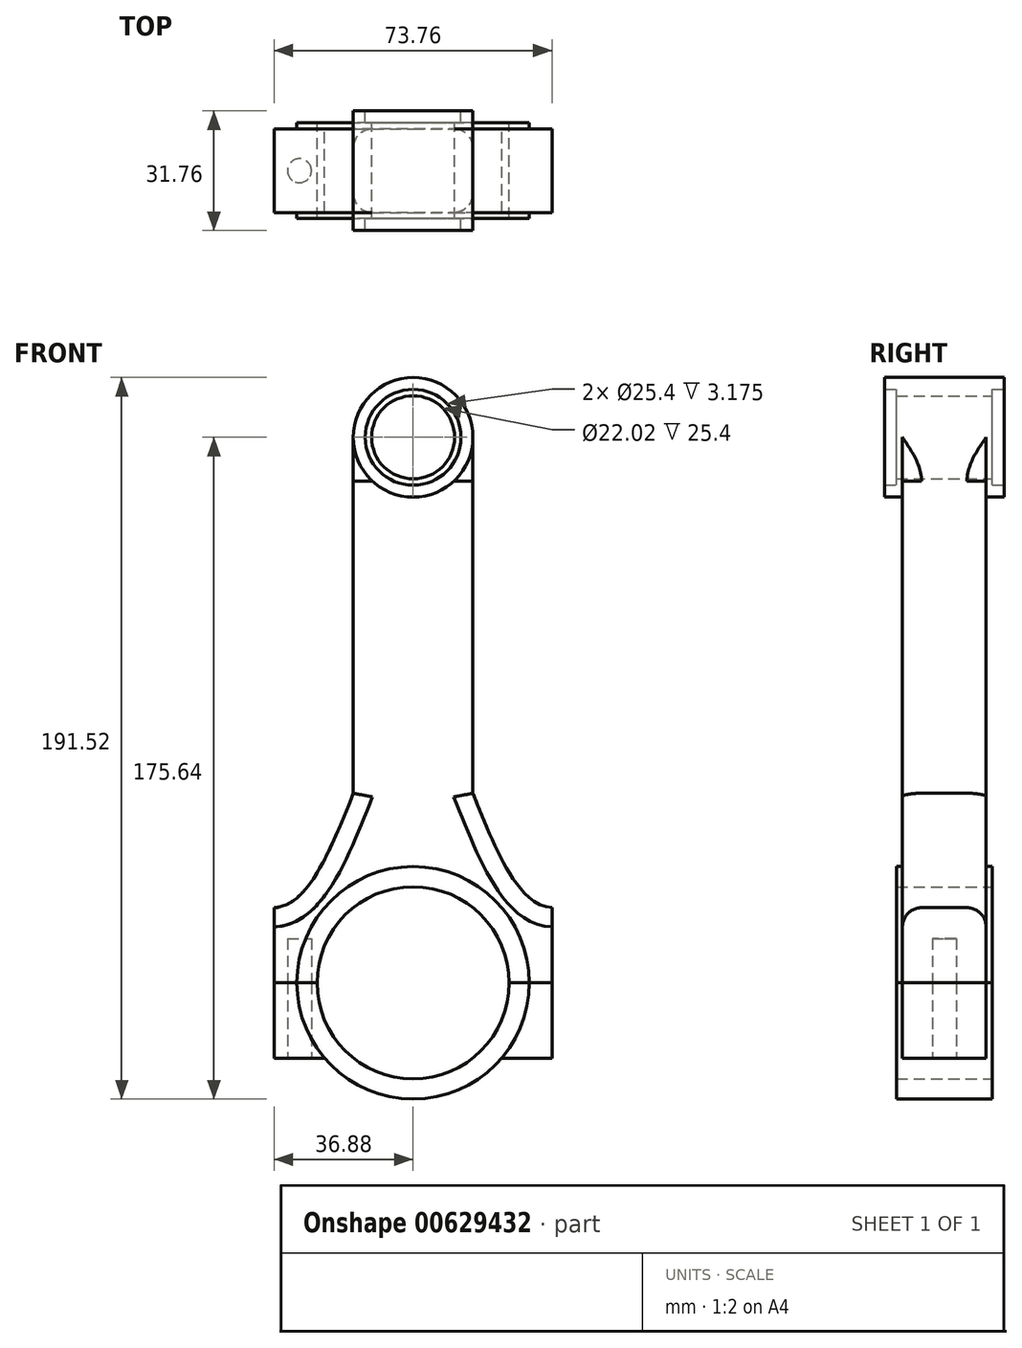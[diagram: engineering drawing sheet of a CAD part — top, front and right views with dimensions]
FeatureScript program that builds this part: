
annotation { "Feature Type Name" : "Feature", "Feature Type Description" : "" }
export const myFeature = defineFeature(function(context is Context, id is Id, definition is map)
    precondition{}
    {
        {
            var Q0;
            Q0=qCreatedBy(makeId("Front.planeOp"),FACE);
            var sketch = newSketch(context, id + "F0", { "sketchPlane" : qUnion([Q0])});
            skCircle(sketch, "E0", {"center": v(0, 0) * mm, "radius": 25.5 * mm});
            skCircle(sketch, "E1", {"center": v(0, 144.78) * mm, "radius": 11.01 * mm});
            skCircle(sketch, "E2", {"center": v(0, 144.78) * mm, "radius": 12.7 * mm});
            skCircle(sketch, "E3", {"center": v(0, 144.78) * mm, "radius": 15.88 * mm});
            skLineSegment(sketch, "E4", {"start": v(15.88, 144.78) * mm, "end": v(15.88, 50.32) * mm});
            skLineSegment(sketch, "E5", {"start": v(-15.88, 144.78) * mm, "end": v(-15.87, 50.32) * mm});
            skLineSegment(sketch, "E6.top", {"start": v(32.06, -19.96) * mm, "end": v(23.54, -19.96) * mm});
            skCircle(sketch, "E7", {"center": v(0, 0) * mm, "radius": 30.86 * mm});
            skPoint(sketch, "E8.orphan", {"position": v(15.88, 19.96) * mm});
            skLineSegment(sketch, "E9.trimOffspring", {"start": v(-23.54, -19.96) * mm, "end": v(-32.06, -19.96) * mm});
            skLineSegment(sketch, "E10.bottom", {"start": v(36.88, -19.96) * mm, "end": v(23.54, -19.96) * mm});
            skLineSegment(sketch, "E10.left", {"start": v(36.88, -19.96) * mm, "end": v(36.88, 19.96) * mm});
            skLineSegment(sketch, "E10.right", {"start": v(-36.88, -19.96) * mm, "end": v(-36.88, 19.96) * mm});
            skPoint(sketch, "E6.right.start.orphan", {"position": v(-32.06, 19.96) * mm});
            skFitSpline(sketch, "E11", {"points": [v(-15.87, 50.32) * mm, v(-36.88, 19.96) * mm, v(-54.21, 32.97) * mm, v(-52.7, 39.53) * mm], "startDerivative": vector(-39.39, -98.54) * mm, "endDerivative": vector(18.96, 28.68) * mm});
            skFitSpline(sketch, "E12.MirrorCS", {"points": [v(15.87, 50.32) * mm, v(36.88, 19.96) * mm, v(54.21, 32.97) * mm, v(52.7, 39.53) * mm], "startDerivative": vector(39.39, -98.54) * mm, "endDerivative": vector(-18.96, 28.68) * mm});
            skPoint(sketch, "E13.1.internal.orphan", {"position": v(32.06, 19.96) * mm});
            skPoint(sketch, "E13.2.internal.orphan", {"position": v(59.54, 19.96) * mm});
            skLineSegment(sketch, "E14.trimOffspring", {"start": v(-23.54, -19.96) * mm, "end": v(-36.88, -19.96) * mm});
            skSolve(sketch);
        }
        {
            var Q0;
            Q0=makeQuery(id+"F0.imprint","IMPRINT",FACE,{"disambiguationData":[TD([[makeQuery(id+"F0.imprint","IMPRINT",EDGE,{"derivedFrom":sQuery(id+"F0.wireOp",EDGE,"E0")}),-1.0]])]});
            extrude(context, id + "F1", {"entities" : qUnion([Q0]), "depth" : 25.4 * mm, "offsetDistance" : 25.4 * mm, "symmetric" : true});
        }
        {
            var Q0;
            {var subQ6=sQuery(id+"F0.wireOp",EDGE,"E4");Q0=makeQuery(id+"F0.imprint","IMPRINT",FACE,{"disambiguationData":[TD([[makeQuery(id+"F0.imprint","IMPRINT",EDGE,{"derivedFrom":subQ6}),-1.0]])]});}
            extrude(context, id + "F2", {"entities" : qUnion([Q0]), "operationType" : NewBodyOperationType.ADD, "depth" : 22.22 * mm, "offsetDistance" : 25.4 * mm, "symmetric" : true});
        }
        {
            var Q0;
            Q0=makeQuery(id+"F0.imprint","IMPRINT",FACE,{"disambiguationData":[TD([[makeQuery(id+"F0.imprint","IMPRINT",EDGE,{"derivedFrom":sQuery(id+"F0.wireOp",EDGE,"E2")}),-1.0]])]});
            extrude(context, id + "F3", {"entities" : qUnion([Q0]), "operationType" : NewBodyOperationType.ADD, "depth" : 31.75 * mm, "offsetDistance" : 25.4 * mm, "symmetric" : true});
        }
        {
            var Q0;
            Q0=makeQuery(id+"F0.imprint","IMPRINT",FACE,{"disambiguationData":[TD([[makeQuery(id+"F0.imprint","IMPRINT",EDGE,{"derivedFrom":sQuery(id+"F0.wireOp",EDGE,"E1")}),-1.0]])]});
            extrude(context, id + "F4", {"entities" : qUnion([Q0]), "operationType" : NewBodyOperationType.ADD, "depth" : 25.4 * mm, "offsetDistance" : 25.4 * mm, "symmetric" : true});
        }
        {
            var Q0;
            Q0=makeQuery(id+"F2.opExtrude","CAP_EDGE",EDGE,{"disambiguationData":[OSD([sQuery(id+"F0.wireOp",EDGE,"E5")])],"isStart":false});
            var Q1;
            Q1=makeQuery(id+"F2.opExtrude","CAP_EDGE",EDGE,{"disambiguationData":[OSD([sQuery(id+"F0.wireOp",EDGE,"E5")])],"isStart":true});
            var Q2;
            Q2=makeQuery(id+"F2.opExtrude","CAP_EDGE",EDGE,{"disambiguationData":[OSD([sQuery(id+"F0.wireOp",EDGE,"E4")])],"isStart":false});
            var Q3;
            Q3=makeQuery(id+"F2.opExtrude","CAP_EDGE",EDGE,{"disambiguationData":[OSD([sQuery(id+"F0.wireOp",EDGE,"E4")])],"isStart":true});
            var Q4;
            Q4=makeQuery(id+"F2.opExtrude","CAP_EDGE",EDGE,{"disambiguationData":[OSD([sQuery(id+"F0.wireOp",EDGE,"E11")])],"isStart":false});
            var Q5;
            Q5=makeQuery(id+"F2.opExtrude","CAP_EDGE",EDGE,{"disambiguationData":[OSD([sQuery(id+"F0.wireOp",EDGE,"E11")])],"isStart":true});
            var Q6;
            Q6=makeQuery(id+"F2.opExtrude","CAP_EDGE",EDGE,{"disambiguationData":[OSD([sQuery(id+"F0.wireOp",EDGE,"E12.MirrorCS")])],"isStart":true});
            var Q7;
            Q7=makeQuery(id+"F2.opExtrude","CAP_EDGE",EDGE,{"disambiguationData":[OSD([sQuery(id+"F0.wireOp",EDGE,"E12.MirrorCS")])],"isStart":false});
            fillet(context, id + "F5", {"entities" : qUnion([Q0, Q1, Q2, Q3, Q4, Q5, Q6, Q7]), "radius" : 5.08 * mm, "tangentPropagation" : true, "allowEdgeOverflow" : false});
        }
        {
            var Q0;
            Q0=makeQuery(id+"F2.opExtrude","SWEPT_FACE",FACE,{"disambiguationData":[OSD([sQuery(id+"F0.wireOp",EDGE,"E14.trimOffspring")])]});
            var sketch = newSketch(context, id + "F6", { "sketchPlane" : qUnion([Q0])});
            skCircle(sketch, "E15", {"center": v(-30.19, 0) * mm, "radius": 3.18 * mm});
            skCircle(sketch, "E16.MirrorC", {"center": v(30.19, 0) * mm, "radius": 3.18 * mm});
            skSolve(sketch);
        }
        {
            var Q0;
            Q0=makeQuery(id+"F6.imprint","IMPRINT",FACE,{"disambiguationData":[TD([[makeQuery(id+"F6.imprint","IMPRINT",EDGE,{"derivedFrom":sQuery(id+"F6.wireOp",EDGE,"E15")}),1.0]])]});
            var Q1;
            Q1=makeQuery(id+"F6.imprint","IMPRINT",FACE,{"disambiguationData":[TD([[makeQuery(id+"F6.imprint","IMPRINT",EDGE,{"derivedFrom":sQuery(id+"F6.wireOp",EDGE,"E16.MirrorC")}),-1.0]])]});
            extrude(context, id + "F7", {"entities" : qUnion([Q0, Q1]), "operationType" : NewBodyOperationType.REMOVE, "oppositeDirection" : true, "depth" : 31.75 * mm, "offsetDistance" : 25.4 * mm});
        }
        {
            var Q0;
            Q0=qCreatedBy(makeId("Front.planeOp"),FACE);
            var sketch = newSketch(context, id + "F8", { "sketchPlane" : qUnion([Q0])});
            skLineSegment(sketch, "E17.bottom", {"start": v(63.72, -0.01) * mm, "end": v(-63.72, -0.01) * mm});
            skLineSegment(sketch, "E17.top", {"start": v(63.72, 0.01) * mm, "end": v(-63.72, 0.01) * mm});
            skLineSegment(sketch, "E17.left", {"start": v(63.72, -0.01) * mm, "end": v(63.72, 0.01) * mm});
            skLineSegment(sketch, "E17.right", {"start": v(-63.72, -0.01) * mm, "end": v(-63.72, 0.01) * mm});
            skPoint(sketch, "E17.middle", {"position": v(0, 0) * mm});
            skSolve(sketch);
        }
        {
            var Q0;
            Q0 = qSketchRegion(id + "F8", true);
            extrude(context, id + "F9", {"entities" : qUnion([Q0]), "operationType" : NewBodyOperationType.REMOVE, "oppositeDirection" : true, "depth" : 38.1 * mm, "offsetDistance" : 25.4 * mm, "symmetric" : true});
        }
    });
